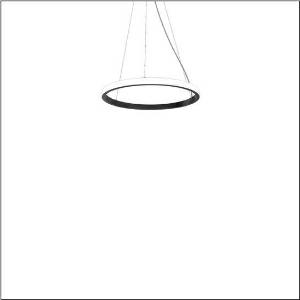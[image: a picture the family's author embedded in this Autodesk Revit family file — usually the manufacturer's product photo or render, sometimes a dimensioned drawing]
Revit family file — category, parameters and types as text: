
# Revit family: silica_r__21_ring-o_5pjbo1d1104a_1dcd
name_source: partatom
category: Lighting Fixtures
units: mm (PartAtom-declared; Revit-internal decimal feet)

## family parameters
Cut with Voids When Loaded = No
Host = Face
Light Source = No
Part Type = Normal
Room Calculation Point = No
Round Connector Dimension = Use Diameter
Shared = No

## types (1)
- Silica® 21 Ring-O (1 x LED, 3740 lm, 60 W, 3000K)
    Apparent Load = 60 VA
    CIE Flux Codes = 2 16 49 50 100
    Color Rendering = 80
    Color Temperature = 3000K
    Default Elevation = 1800 mm
    Description = Silica® 21 Ring-O, suspended luminaire, of PMMA, frosted, light emission: outer ring side luminous distribution, primary light characteristic: symmetric, installation type: suspended mounting, LED, rated luminous flux: 3.744lm, luminous efficacy: 62lm/W, light colour: 830, colour temperature: 3000K, control gear: DALI 2, with terminal, 5-pole, mains connection: 230V, AC/DC, 0/50..60Hz, rated input power: 60W, housing, of extruded aluminium section, jet black (RAL 9005), diameter: 610mm, ceiling canopy, jet black (RAL 9005), protection rating (lamp compartment): IP40, insulation class (complete): insulation class I (protective earthing), certification: CE, impact resistance: IK02, permissible operating ambient temperature: 0..+35°C, packaging unit: 1 piece
    Height = 48 mm  [stored 0.15748 ft]
    Lamp = 1 x LED
    Lamp Light Flux = 3740 lm
    Lamp Power = 60 W
    Lamp count = 1
    Length = 610 mm
    Luminous efficacy = 62 lm/W
    Manufacturer = Siteco
    ModVariant = No
    Model = 5PJBO1D1104A
    Mounting Place = Ceiling
    Mounting Type = Pendant
    Number of Poles = 1
    OnlyDefault = Yes
    Power Factor = 1
    Product Name = Silica® 21 Ring-O
    Product group = suspended luminaire
    ProductGroupID = 904
    Protection Class = Protection class I
    Protection Degree = IP 40
    RLX_Detail_Level = 1
    RLX_Emergency_Light_Flux = 0 lm
    RLX_Emergency_Type = 0
    RLX_Emergency_Type_DB = No
    RlxData = <blob elided: 12173 chars, md5=8148262c>
    Socket = socket
    Standby Power = 0 W
    System Light Flux = 3740 lm
    System Power = 60 W
    Type Comments = Product without accessories
    Type Image = l_1258377.jpg
    URL = http://relux.com
    VarID = ---
    Voltage = 0 V
    Weight = 0.00 kg
    Width = 0 mm  [stored 0 ft]

note: [stored X ft] marks values corroborated as IEEE doubles in the binary element streams (Revit-internal decimal feet)

## geometry (parser evidence)
native form markers: Sweep x13
no freeform markers — native parametric forms only
